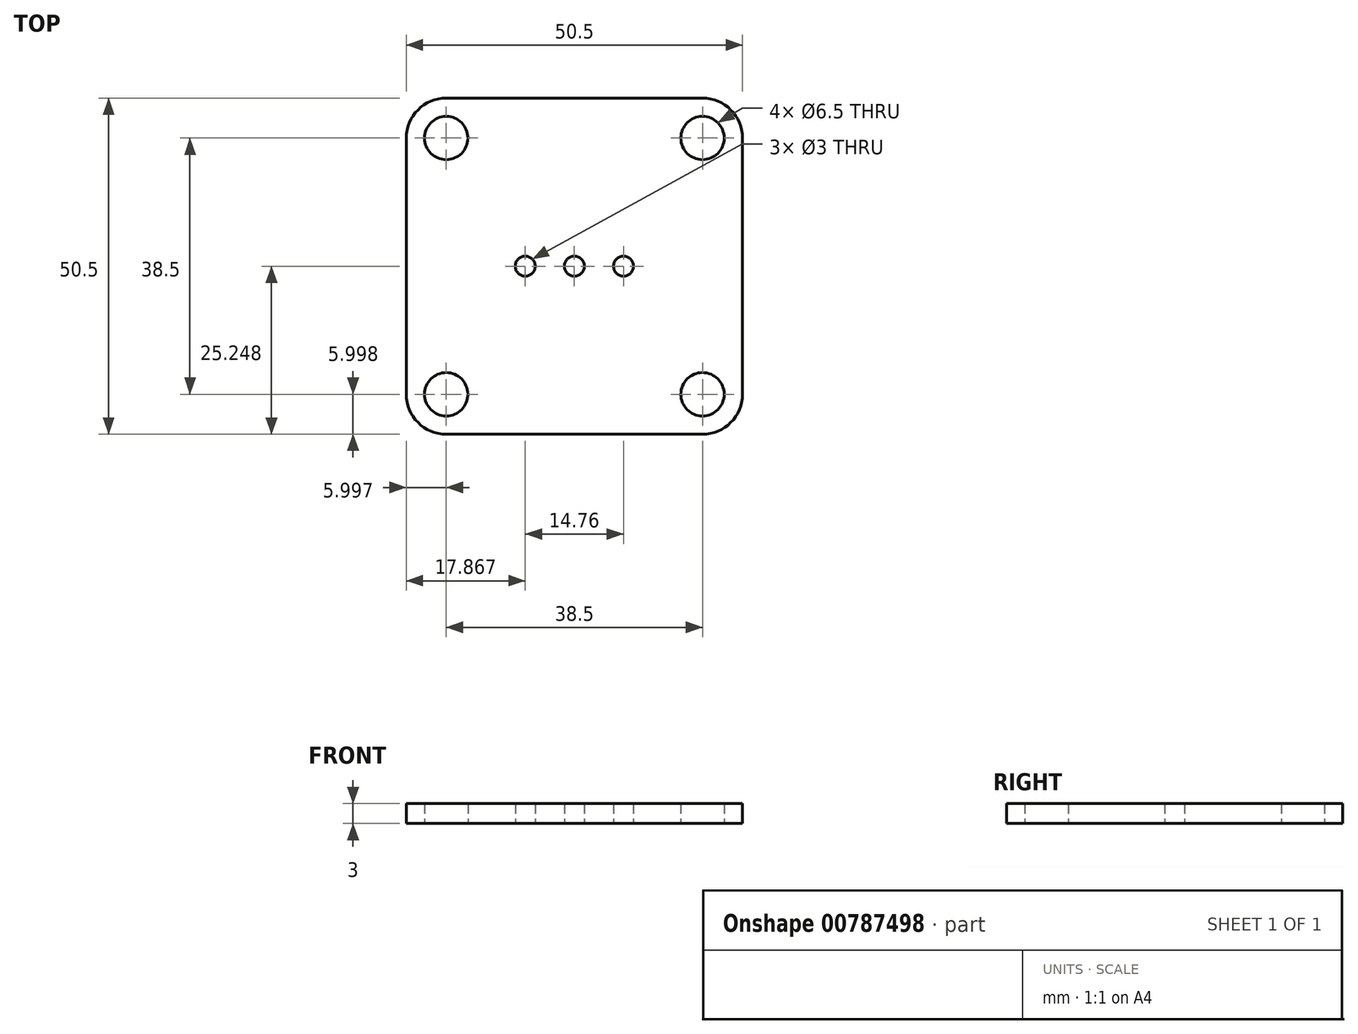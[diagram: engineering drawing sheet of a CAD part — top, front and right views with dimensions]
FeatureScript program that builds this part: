
annotation { "Feature Type Name" : "Feature", "Feature Type Description" : "" }
export const myFeature = defineFeature(function(context is Context, id is Id, definition is map)
    precondition{}
    {
        {
            var Q0;
            Q0=qCreatedBy(makeId("Top.planeOp"),FACE);
            var sketch = newSketch(context, id + "F0", { "sketchPlane" : qUnion([Q0])});
            skLineSegment(sketch, "E0.bottom", {"start": v(-51.73, 17.16) * mm, "end": v(-13.23, 17.16) * mm});
            skLineSegment(sketch, "E0.top", {"start": v(-51.73, -33.34) * mm, "end": v(-13.23, -33.34) * mm});
            skLineSegment(sketch, "E0.left", {"start": v(-57.73, 11.16) * mm, "end": v(-57.73, -27.34) * mm});
            skLineSegment(sketch, "E0.right", {"start": v(-7.23, 11.16) * mm, "end": v(-7.23, -27.34) * mm});
            skCircle(sketch, "E1", {"center": v(-32.48, -8.1) * mm, "radius": 1.5 * mm});
            skPoint(sketch, "E1.centerSnap0", {"position": v(-32.48, 17.16) * mm});
            skPoint(sketch, "E1.centerSnap1", {"position": v(-57.73, -8.1) * mm});
            skCircle(sketch, "E2", {"center": v(-25.1, -8.1) * mm, "radius": 1.5 * mm});
            skCircle(sketch, "E3", {"center": v(-39.86, -8.1) * mm, "radius": 1.5 * mm});
            skPoint(sketch, "E4.visualSharp", {"position": v(-57.73, 17.16) * mm});
            skArc(sketch, "E4.filletArc", {"start": v(-51.73, 17.16) * mm, "mid": v(-55.98, 15.4) * mm, "end": v(-57.73, 11.16) * mm});
            skPoint(sketch, "E5.visualSharp", {"position": v(-7.23, 17.16) * mm});
            skArc(sketch, "E5.filletArc", {"start": v(-7.23, 11.16) * mm, "mid": v(-9, 15.4) * mm, "end": v(-13.23, 17.16) * mm});
            skPoint(sketch, "E6.visualSharp", {"position": v(-7.23, -33.34) * mm});
            skArc(sketch, "E6.filletArc", {"start": v(-13.23, -33.34) * mm, "mid": v(-9, -31.58) * mm, "end": v(-7.23, -27.34) * mm});
            skPoint(sketch, "E7.visualSharp", {"position": v(-57.73, -33.34) * mm});
            skArc(sketch, "E7.filletArc", {"start": v(-57.73, -27.34) * mm, "mid": v(-55.98, -31.58) * mm, "end": v(-51.73, -33.34) * mm});
            skCircle(sketch, "E8", {"center": v(-51.73, 11.16) * mm, "radius": 3.25 * mm});
            skCircle(sketch, "E9", {"center": v(-13.23, 11.16) * mm, "radius": 3.25 * mm});
            skCircle(sketch, "E10", {"center": v(-13.23, -27.34) * mm, "radius": 3.25 * mm});
            skCircle(sketch, "E11", {"center": v(-51.73, -27.34) * mm, "radius": 3.25 * mm});
            skSolve(sketch);
        }
        {
            var Q0;
            Q0=makeQuery(id+"F0.imprint","IMPRINT",FACE,{"disambiguationData":[TD([[makeQuery(id+"F0.imprint","IMPRINT",EDGE,{"derivedFrom":sQuery(id+"F0.wireOp",EDGE,"E0.bottom")}),-1.0]])]});
            extrude(context, id + "F1", {"entities" : qUnion([Q0]), "depth" : 3 * mm, "offsetDistance" : 25.4 * mm});
        }
    });
